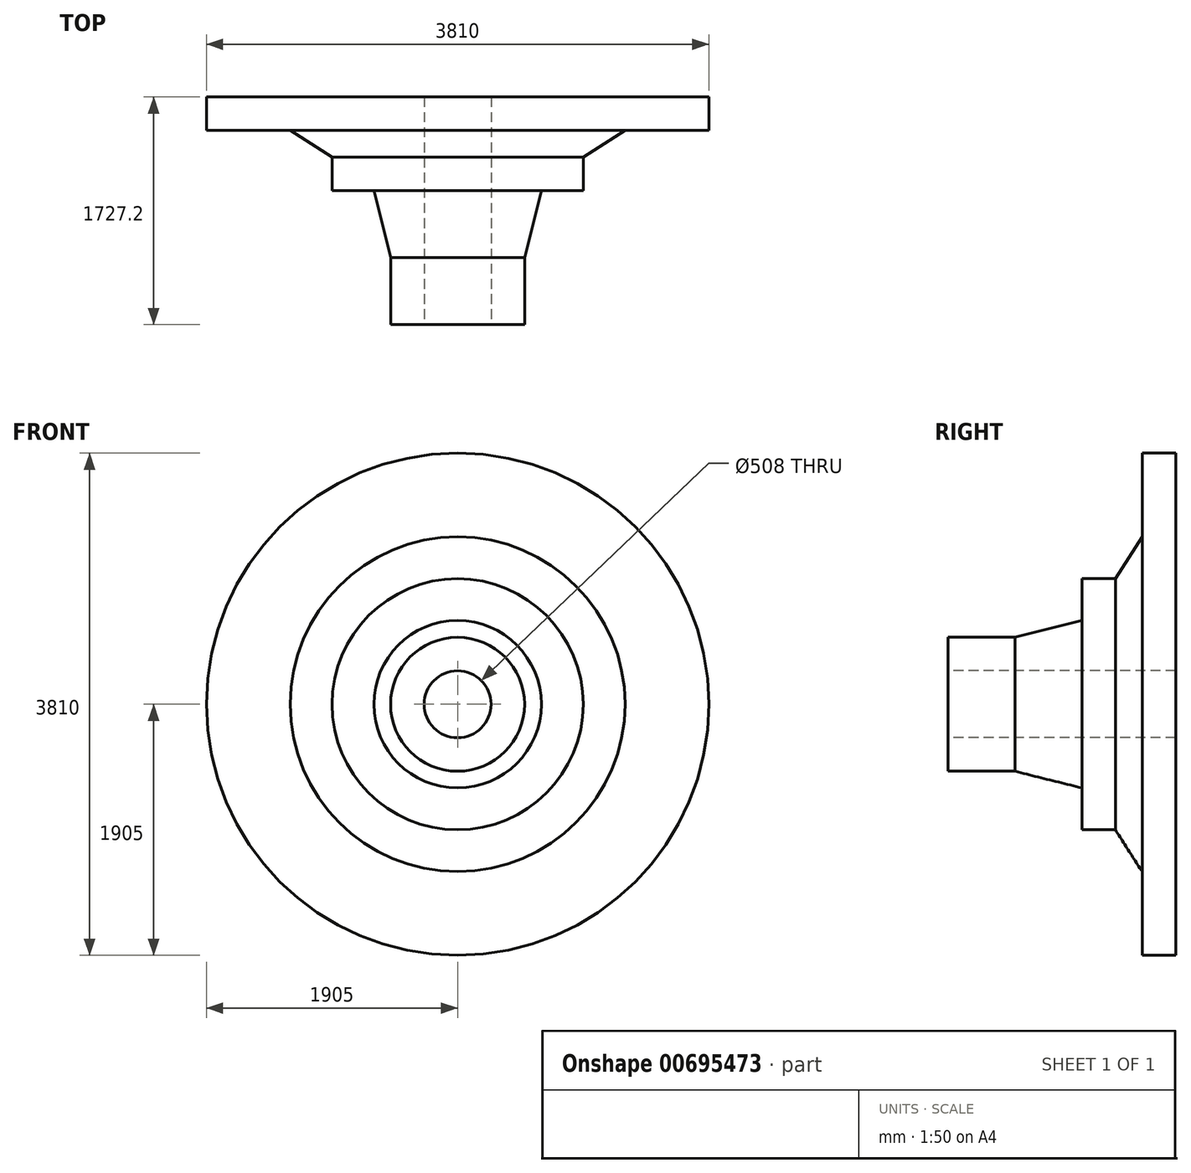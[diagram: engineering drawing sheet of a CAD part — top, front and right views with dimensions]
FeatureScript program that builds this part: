
annotation { "Feature Type Name" : "Feature", "Feature Type Description" : "" }
export const myFeature = defineFeature(function(context is Context, id is Id, definition is map)
    precondition{}
    {
        {
            var Q0;
            Q0=qCreatedBy(makeId("Right.planeOp"),FACE);
            var sketch = newSketch(context, id + "F0", { "sketchPlane" : qUnion([Q0])});
            skLineSegment(sketch, "E0", {"start": v(0, 0) * mm, "end": v(0, -1905) * mm});
            skLineSegment(sketch, "E1", {"start": v(0, -1905) * mm, "end": v(-254, -1905) * mm});
            skLineSegment(sketch, "E2", {"start": v(-254, -1905) * mm, "end": v(-254, -1270) * mm});
            skPoint(sketch, "E3", {"position": v(-457.2, -952.5) * mm});
            skLineSegment(sketch, "E4", {"start": v(-254, -1270) * mm, "end": v(-457.2, -952.5) * mm});
            skLineSegment(sketch, "E5", {"start": v(-457.2, -952.5) * mm, "end": v(-711.2, -952.5) * mm});
            skLineSegment(sketch, "E6", {"start": v(-711.2, -952.5) * mm, "end": v(-711.2, -635) * mm});
            skPoint(sketch, "E7", {"position": v(-1219.2, -508) * mm});
            skLineSegment(sketch, "E8", {"start": v(-711.2, -635) * mm, "end": v(-1219.2, -508) * mm});
            skLineSegment(sketch, "E9", {"start": v(-1219.2, -508) * mm, "end": v(-1727.2, -508) * mm});
            skLineSegment(sketch, "E10", {"start": v(-1727.2, -508) * mm, "end": v(-1727.2, 0) * mm});
            skLineSegment(sketch, "E11", {"start": v(-1727.2, 0) * mm, "end": v(0, 0) * mm});
            skSolve(sketch);
        }
        {
            var Q0;
            Q0=makeQuery(id+"F0.imprint","IMPRINT",FACE,{"disambiguationData":[TD([[makeQuery(id+"F0.imprint","IMPRINT",EDGE,{"derivedFrom":sQuery(id+"F0.wireOp",EDGE,"E0")}),-1.0]])]});
            var Q1;
            Q1=sQuery(id+"F0.wireOp",EDGE,"E11");
            revolve(context, id + "F1", {"surfaceOperationType" : NewSurfaceOperationType.NEW, "entities" : qUnion([Q0]), "axis" : qUnion([Q1]), "revolveType" : RevolveType.FULL});
        }
        {
            var Q0;
            Q0=makeQuery(id+"F1.opRevolve","SWEPT_FACE",FACE,{"disambiguationData":[OSD([sQuery(id+"F0.wireOp",EDGE,"E10")])]});
            var sketch = newSketch(context, id + "F2", { "sketchPlane" : qUnion([Q0])});
            skCircle(sketch, "E12", {"center": v(0, 0) * mm, "radius": 254 * mm});
            skSolve(sketch);
        }
        {
            var Q0;
            Q0=makeQuery(id+"F2.imprint","IMPRINT",FACE,{"disambiguationData":[TD([[makeQuery(id+"F2.imprint","IMPRINT",EDGE,{"derivedFrom":sQuery(id+"F2.wireOp",EDGE,"E12")}),1.0]])]});
            extrude(context, id + "F3", {"entities" : qUnion([Q0]), "operationType" : NewBodyOperationType.REMOVE, "endBound" : BoundingType.THROUGH_ALL, "oppositeDirection" : true, "depth" : 25.4 * mm, "offsetDistance" : 25.4 * mm});
        }
    });
